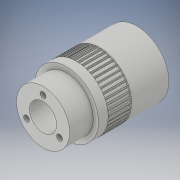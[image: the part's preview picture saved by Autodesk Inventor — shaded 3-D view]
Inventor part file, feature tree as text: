
AUTODESK INVENTOR PART (.ipt)
format: ipt  version: 2018 (Build 220112000, 112)  size: 507,392 bytes
history: native  units: in
note: dims shown in document units (in); Inventor stores cm internally (conversion verified against a paired STEP export)
features: extrude x6, sketch x4, mirror x1, plane x1, fillet x1, other x1, pattern_circular x1
ambient origin geometry x8: Origin, YZ Plane, XZ Plane, XY Plane, X Axis, Y Axis, Z Axis, Center Point
bodies: Solid1 (feature_tree)
feature tree (15):
  sketch  "Sketch1"  dims[d0=0.9843in d1=0.502in]
  extrude  "Extrusion1"  Depth=0.502in
  extrude  "Extrusion2"  Depth=0.6102in
  extrude  "Extrusion3"  Depth=0.1083in
  extrude  "Extrusion4"  Depth=0.0098in
  mirror  "Mirror1"
  plane  "Work Plane1"
  extrude  "Extrusion5"  Depth=1.1811in TaperAngle=0.0deg
  extrude  "Extrusion6"  Depth=0.5512in TaperAngle=0.0deg
  fillet  "Fillet1"  Radius=0.3937in
  other  "Work Axis1"
  pattern_circular  "Circular Pattern1"  Count=2  [1 undecoded]
  sketch  "Sketch2"  dims[d2=0.6102in d3=0.1083in]
  sketch  "Sketch3"  dims[d4=0.1083in d5=0.1083in]
  sketch  "Sketch4"  dims[d6=0.5512in d7=0.0in d8=0.0984in d9=1.1811in d10=0.1181in d11=0.0in d12=0.0in d13=0.5512in d14=0.0in d15=0.3937in d16=0.7874in d17=0.3937in d18=0.7874in d19=0.7874in d20=0.0in d21=1.1811in d22=-0.3937in d23=1.1276in d24=1.1811in d25=0.4331in d26=0.0in d28=0.0276in d29=0.4331in d30=0.0in d31=0.0098in d32=17.7165in d33=360.0deg]
note: 1 required parameter value undecoded (feature->parameter linkage not recoverable at this tier; creation-order binding heuristic only, values carry confidence <= 0.55)
